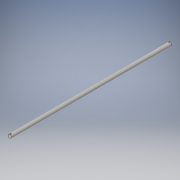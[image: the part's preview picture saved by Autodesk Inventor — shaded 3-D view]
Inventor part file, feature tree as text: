
AUTODESK INVENTOR PART (.ipt)
format: ipt  version: 2016 (Build 200138000, 138)  size: 102,400 bytes
history: native  units: in
note: dims shown in document units (in); Inventor stores cm internally (conversion verified against a paired STEP export)
features: extrude x2, sketch x2
ambient origin geometry x8: Origin, YZ Plane, XZ Plane, XY Plane, X Axis, Y Axis, Z Axis, Center Point
bodies: Solid1 (feature_tree)
feature tree (4):
  extrude  "Extrusion1"  Depth=11.3137in TaperAngle=0.0deg
  extrude  "Extrusion2"  Depth=0.06in
  sketch  "Sketch1"  dims[d0=0.25in d1=11.3137in d2=0.0in]
  sketch  "Sketch2"  dims[d3=0.06in d4=0.1in d5=0.06in d6=0.1in d7=0.3in d8=0.0in]
